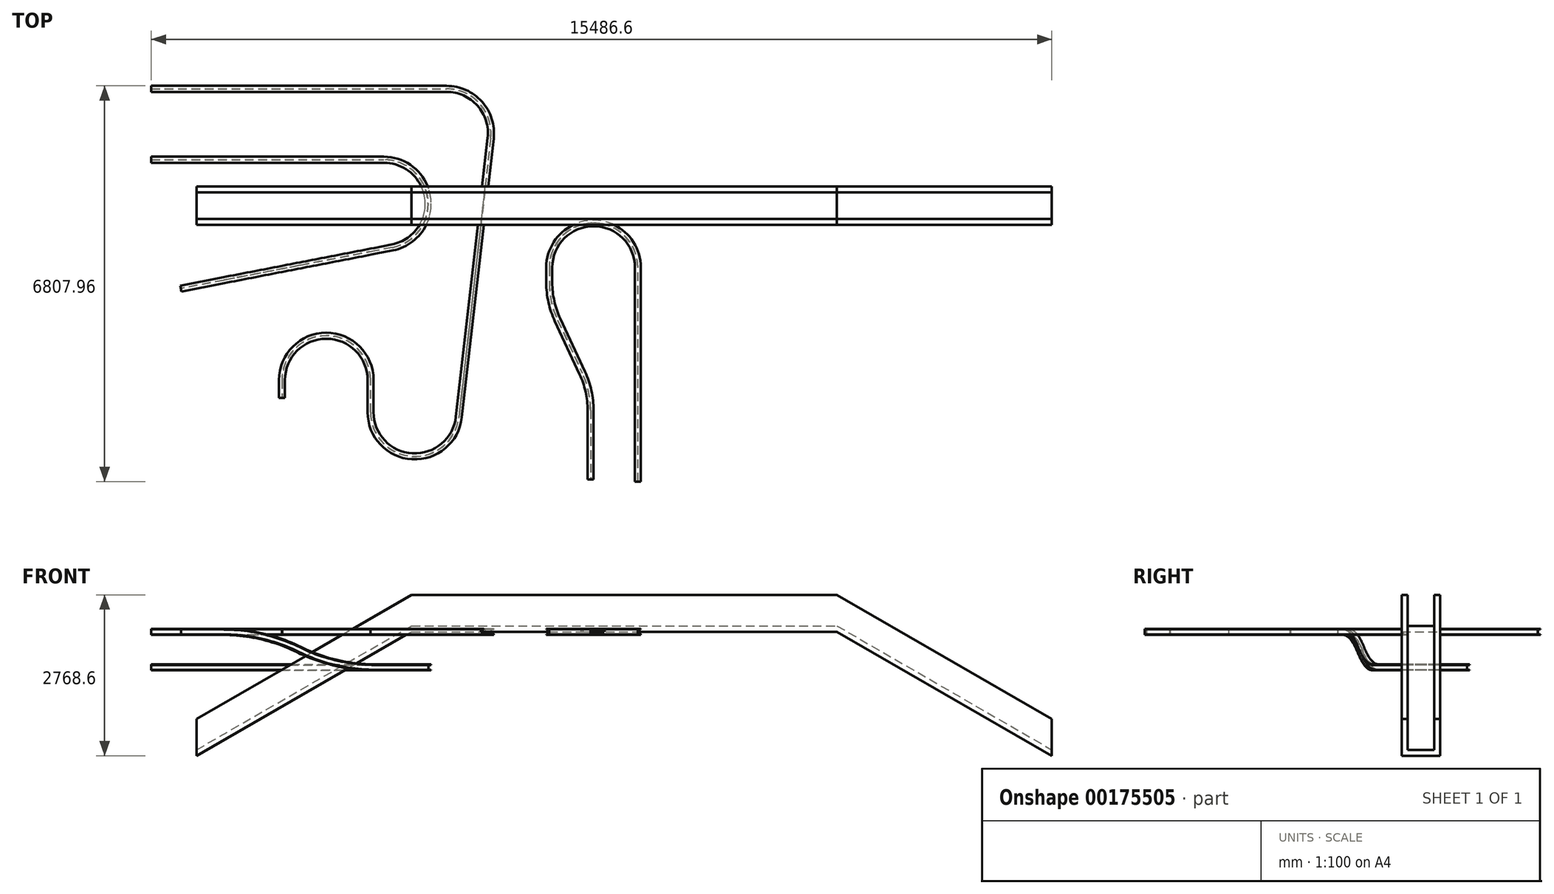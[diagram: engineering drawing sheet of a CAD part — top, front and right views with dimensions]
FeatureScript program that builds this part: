
annotation { "Feature Type Name" : "Feature", "Feature Type Description" : "" }
export const myFeature = defineFeature(function(context is Context, id is Id, definition is map)
    precondition{}
    {
        {
            var Q0;
            Q0=qCreatedBy(makeId("Right.planeOp"),FACE);
            var sketch = newSketch(context, id + "F0", { "sketchPlane" : qUnion([Q0])});
            skLineSegment(sketch, "E0", {"start": v(-3.56, -43.3) * mm, "end": v(-3.56, 43.3) * mm});
            skLineSegment(sketch, "E1", {"start": v(-3.56, 43.3) * mm, "end": v(-51.56, 43.3) * mm});
            skLineSegment(sketch, "E2", {"start": v(-51.56, 43.3) * mm, "end": v(-51.56, 52.83) * mm});
            skLineSegment(sketch, "E3", {"start": v(-51.56, 52.83) * mm, "end": v(51.56, 52.83) * mm});
            skLineSegment(sketch, "E4", {"start": v(51.56, 52.83) * mm, "end": v(51.56, 43.3) * mm});
            skLineSegment(sketch, "E5", {"start": v(51.56, 43.3) * mm, "end": v(3.56, 43.3) * mm});
            skLineSegment(sketch, "E6", {"start": v(3.56, 43.3) * mm, "end": v(3.56, -43.3) * mm});
            skLineSegment(sketch, "E7", {"start": v(3.56, -43.3) * mm, "end": v(51.56, -43.3) * mm});
            skLineSegment(sketch, "E8", {"start": v(51.56, -43.3) * mm, "end": v(51.56, -52.83) * mm});
            skLineSegment(sketch, "E9", {"start": v(51.56, -52.83) * mm, "end": v(-51.56, -52.83) * mm});
            skLineSegment(sketch, "E10", {"start": v(-51.56, -52.83) * mm, "end": v(-51.56, -43.3) * mm});
            skLineSegment(sketch, "E11", {"start": v(-51.56, -43.3) * mm, "end": v(-3.56, -43.3) * mm});
            skSolve(sketch);
        }
        {
            var Q0;
            Q0=qCreatedBy(makeId("Top.planeOp"),FACE);
            var sketch = newSketch(context, id + "F1", { "sketchPlane" : qUnion([Q0])});
            skLineSegment(sketch, "E12", {"start": v(0, 0) * mm, "end": v(5080, 0) * mm});
            skArc(sketch, "E13", {"start": v(5837.12, -848.13) * mm, "mid": v(5648.45, -254.55) * mm, "end": v(5080, 0) * mm});
            skPoint(sketch, "E14", {"position": v(4533.9, -5562.6) * mm});
            skArc(sketch, "E15", {"start": v(3771.9, -5562.6) * mm, "mid": v(4490.77, -6323.38) * mm, "end": v(5291.02, -5648.73) * mm});
            skLineSegment(sketch, "E16", {"start": v(5837.12, -848.13) * mm, "end": v(5291.02, -5648.73) * mm});
            skLineSegment(sketch, "E17", {"start": v(4533.9, -5562.6) * mm, "end": v(3553.98, -5562.6) * mm, "construction": true});
            skPoint(sketch, "E18", {"position": v(3009.9, -5010.15) * mm});
            skLineSegment(sketch, "E19", {"start": v(3771.9, -5562.6) * mm, "end": v(3771.9, -5010.15) * mm});
            skArc(sketch, "E20", {"start": v(3771.9, -5010.15) * mm, "mid": v(3009.9, -4248.15) * mm, "end": v(2247.9, -5010.15) * mm});
            skLineSegment(sketch, "E21", {"start": v(2247.9, -5010.15) * mm, "end": v(2247.9, -5314.95) * mm});
            skSolve(sketch);
        }
        {
            var Q0;
            Q0 = qSketchRegion(id + "F0", true);
            var Q1;
            Q1=sQuery(id+"F1.wireOp",EDGE,"E12");
            var Q2;
            Q2=sQuery(id+"F1.wireOp",EDGE,"E13");
            var Q3;
            Q3=sQuery(id+"F1.wireOp",EDGE,"E16");
            var Q4;
            Q4=sQuery(id+"F1.wireOp",EDGE,"E15");
            var Q5;
            Q5=sQuery(id+"F1.wireOp",EDGE,"E19");
            var Q6;
            Q6=sQuery(id+"F1.wireOp",EDGE,"E20");
            var Q7;
            Q7=sQuery(id+"F1.wireOp",EDGE,"E21");
            sweep(context, id + "F2", {"profiles" : qUnion([Q0]), "path" : qUnion([Q1, Q2, Q3, Q4, Q5, Q6, Q7])});
        }
        {
            var Q0;
            Q0=qCreatedBy(makeId("Right.planeOp"),FACE);
            var sketch = newSketch(context, id + "F3", { "sketchPlane" : qUnion([Q0])});
            skLineSegment(sketch, "E22", {"start": v(-1219.2, 399.7) * mm, "end": v(-1219.2, -446.14) * mm, "construction": true});
            skLineSegment(sketch, "E23", {"start": v(-902.69, 0) * mm, "end": v(-1653.95, 0) * mm, "construction": true});
            skLineSegment(sketch, "E24", {"start": v(-1215.64, -652.9) * mm, "end": v(-1167.64, -652.9) * mm});
            skLineSegment(sketch, "E25", {"start": v(-1167.64, -662.43) * mm, "end": v(-1167.64, -652.9) * mm});
            skLineSegment(sketch, "E26", {"start": v(-1167.64, -662.43) * mm, "end": v(-1270.76, -662.43) * mm});
            skLineSegment(sketch, "E27", {"start": v(-1270.76, -652.9) * mm, "end": v(-1270.76, -662.43) * mm});
            skLineSegment(sketch, "E28", {"start": v(-1270.76, -652.9) * mm, "end": v(-1222.76, -652.9) * mm});
            skLineSegment(sketch, "E29", {"start": v(-1222.76, -570.36) * mm, "end": v(-1270.76, -570.36) * mm});
            skLineSegment(sketch, "E30", {"start": v(-1270.76, -560.83) * mm, "end": v(-1270.76, -570.36) * mm});
            skLineSegment(sketch, "E31", {"start": v(-1270.76, -560.83) * mm, "end": v(-1167.64, -560.83) * mm});
            skLineSegment(sketch, "E32", {"start": v(-1167.64, -570.36) * mm, "end": v(-1167.64, -560.83) * mm});
            skLineSegment(sketch, "E33", {"start": v(-1167.64, -570.36) * mm, "end": v(-1215.64, -570.36) * mm});
            skLineSegment(sketch, "E34", {"start": v(-1215.64, -570.36) * mm, "end": v(-1215.64, -652.9) * mm});
            skLineSegment(sketch, "E35", {"start": v(-1222.76, -570.36) * mm, "end": v(-1222.76, -652.9) * mm});
            skSolve(sketch);
        }
        {
            var Q0;
            Q0=qCreatedBy(makeId("Top.planeOp"),FACE);
            var sketch = newSketch(context, id + "F4", { "sketchPlane" : qUnion([Q0])});
            skLineSegment(sketch, "E36", {"start": v(0, -1219.2) * mm, "end": v(4000.5, -1219.2) * mm});
            skPoint(sketch, "E37", {"position": v(5080, -762) * mm});
            skArc(sketch, "E38", {"start": v(4145.9, -2729.2) * mm, "mid": v(4759, -1908.17) * mm, "end": v(4000.5, -1219.2) * mm});
            skLineSegment(sketch, "E39", {"start": v(4145.9, -2729.2) * mm, "end": v(3846.7, -2787.36) * mm});
            skLineSegment(sketch, "E40", {"start": v(4000.5, -1981.2) * mm, "end": v(4000.5, -3343.17) * mm, "construction": true});
            skLineSegment(sketch, "E41", {"start": v(4000.5, -1981.2) * mm, "end": v(4145.9, -2729.2) * mm, "construction": true});
            skSolve(sketch);
        }
        {
            var Q0;
            Q0 = qSketchRegion(id + "F3", true);
            var Q1;
            Q1=sQuery(id+"F4.wireOp",EDGE,"E36");
            var Q2;
            Q2=sQuery(id+"F4.wireOp",EDGE,"E38");
            var Q3;
            Q3=sQuery(id+"F4.wireOp",EDGE,"E39");
            sweep(context, id + "F5", {"profiles" : qUnion([Q0]), "path" : qUnion([Q1, Q2, Q3])});
        }
        {
            var Q0;
            Q0=makeQuery(id+"F5.opSweep","SWEPT_FACE",FACE,{"disambiguationData":[OSD([sQuery(id+"F3.wireOp",EDGE,"E34"),sQuery(id+"F4.wireOp",EDGE,"E39")])]});
            var sketch = newSketch(context, id + "F6", { "sketchPlane" : qUnion([Q0])});
            skArc(sketch, "E42", {"start": v(1915.58, -306.83) * mm, "mid": v(2562.62, -534.45) * mm, "end": v(3244.17, -611.63) * mm});
            skLineSegment(sketch, "E43", {"start": v(3244.17, -611.63) * mm, "end": v(3472.86, -611.63) * mm, "construction": true});
            skArc(sketch, "E44", {"start": v(1915.58, -306.83) * mm, "mid": v(1272.56, -80.13) * mm, "end": v(595.23, -2.03) * mm});
            skLineSegment(sketch, "E45", {"start": v(595.23, -2.03) * mm, "end": v(-153.73, 0) * mm});
            skSolve(sketch);
        }
        {
            var Q0;
            Q0=makeQuery(id+"F5.opSweep","CAP_FACE",FACE,{"disambiguationData":[OSD([sQuery(id+"F3.wireOp",EDGE,"E24"),sQuery(id+"F3.wireOp",EDGE,"E25"),sQuery(id+"F3.wireOp",EDGE,"E26"),sQuery(id+"F3.wireOp",EDGE,"E27"),sQuery(id+"F3.wireOp",EDGE,"E28"),sQuery(id+"F3.wireOp",EDGE,"E29"),sQuery(id+"F3.wireOp",EDGE,"E30"),sQuery(id+"F3.wireOp",EDGE,"E31"),sQuery(id+"F3.wireOp",EDGE,"E32"),sQuery(id+"F3.wireOp",EDGE,"E33"),sQuery(id+"F3.wireOp",EDGE,"E34"),sQuery(id+"F3.wireOp",EDGE,"E35"),sQuery(id+"F4.wireOp",VERTEX,"E39.end")])],"isStart":false});
            var Q1;
            Q1=sQuery(id+"F6.wireOp",EDGE,"E42");
            var Q2;
            Q2=sQuery(id+"F6.wireOp",EDGE,"E44");
            var Q3;
            Q3=sQuery(id+"F6.wireOp",EDGE,"E45");
            sweep(context, id + "F7", {"operationType" : NewBodyOperationType.ADD, "profiles" : qUnion([Q0]), "path" : qUnion([Q1, Q2, Q3])});
        }
        {
            var Q0;
            Q0=qCreatedBy(makeId("Front.planeOp"),FACE);
            cPlane(context, id + "F8", {"entities" : qUnion([Q0]), "cplaneType" : CPlaneType.OFFSET, "offset" : 2336.8 * mm, "width" : 152.4 * mm, "height" : 152.4 * mm});
        }
        {
            var Q0;
            Q0=qCreatedBy(id+"F8.planeOp",FACE);
            var sketch = newSketch(context, id + "F9", { "sketchPlane" : qUnion([Q0])});
            skLineSegment(sketch, "E46", {"start": v(781.05, -2131.57) * mm, "end": v(4476.75, 2.03) * mm});
            skLineSegment(sketch, "E47", {"start": v(4476.75, 2.03) * mm, "end": v(11791.95, 2.03) * mm});
            skLineSegment(sketch, "E48", {"start": v(11791.95, 2.03) * mm, "end": v(15487.65, -2131.57) * mm});
            skSolve(sketch);
        }
        {
            var Q0;
            Q0=qCreatedBy(makeId("Right.planeOp"),FACE);
            cPlane(context, id + "F10", {"entities" : qUnion([Q0]), "cplaneType" : CPlaneType.OFFSET, "offset" : 780 * mm, "width" : 152.4 * mm, "height" : 152.4 * mm});
        }
        {
            var Q0;
            Q0=qCreatedBy(id+"F10.planeOp",FACE);
            var sketch = newSketch(context, id + "F11", { "sketchPlane" : qUnion([Q0])});
            skLineSegment(sketch, "E49", {"start": v(-2336.8, -2131.57) * mm, "end": v(-2336.8, -1496.57) * mm});
            skLineSegment(sketch, "E50", {"start": v(-2336.8, -1496.57) * mm, "end": v(-2235.2, -1496.57) * mm});
            skLineSegment(sketch, "E51", {"start": v(-2235.2, -1496.57) * mm, "end": v(-2235.2, -2029.97) * mm});
            skLineSegment(sketch, "E52", {"start": v(-2235.2, -2029.97) * mm, "end": v(-1778, -2029.97) * mm});
            skLineSegment(sketch, "E53", {"start": v(-1778, -2029.97) * mm, "end": v(-1778, -1496.57) * mm});
            skLineSegment(sketch, "E54", {"start": v(-1778, -1496.57) * mm, "end": v(-1676.4, -1496.57) * mm});
            skLineSegment(sketch, "E55", {"start": v(-1676.4, -1496.57) * mm, "end": v(-1676.4, -2131.57) * mm});
            skLineSegment(sketch, "E56", {"start": v(-1676.4, -2131.57) * mm, "end": v(-2336.8, -2131.57) * mm});
            skSolve(sketch);
        }
        {
            var Q0;
            Q0=makeQuery(id+"F11.imprint","IMPRINT",FACE,{"disambiguationData":[TD([[makeQuery(id+"F11.imprint","IMPRINT",EDGE,{"derivedFrom":sQuery(id+"F11.wireOp",EDGE,"E49")}),-1.0]])]});
            var Q1;
            Q1=sQuery(id+"F9.wireOp",EDGE,"E46");
            var Q2;
            Q2=sQuery(id+"F9.wireOp",EDGE,"E47");
            var Q3;
            Q3=sQuery(id+"F9.wireOp",EDGE,"E48");
            sweep(context, id + "F12", {"operationType" : NewBodyOperationType.ADD, "profiles" : qUnion([Q0]), "path" : qUnion([Q1, Q2, Q3]), "keepProfileOrientation" : true});
        }
        {
            var Q0;
            Q0=qCreatedBy(makeId("Top.planeOp"),FACE);
            var sketch = newSketch(context, id + "F13", { "sketchPlane" : qUnion([Q0])});
            skPoint(sketch, "E57", {"position": v(5080, -762) * mm});
            skPoint(sketch, "E58", {"position": v(7607.3, -3073.4) * mm});
            skArc(sketch, "E59", {"start": v(6845.3, -3073.4) * mm, "mid": v(7607.3, -2311.4) * mm, "end": v(8369.3, -3073.4) * mm});
            skLineSegment(sketch, "E60", {"start": v(8369.3, -3073.4) * mm, "end": v(8369.3, -6756.4) * mm});
            skLineSegment(sketch, "E61", {"start": v(6845.3, -3073.4) * mm, "end": v(6845.3, -3332.44) * mm});
            skLineSegment(sketch, "E62", {"start": v(6988.09, -3976.5) * mm, "end": v(7413.17, -4888.1) * mm});
            skLineSegment(sketch, "E63", {"start": v(7555.95, -5532.16) * mm, "end": v(7555.95, -6718.3) * mm});
            skPoint(sketch, "E64.visualSharp", {"position": v(6845.3, -3670.3) * mm});
            skArc(sketch, "E64.filletArc", {"start": v(6845.3, -3332.44) * mm, "mid": v(6881.42, -3662.3) * mm, "end": v(6988.09, -3976.5) * mm});
            skPoint(sketch, "E65.visualSharp", {"position": v(7555.95, -5194.3) * mm});
            skArc(sketch, "E65.filletArc", {"start": v(7555.95, -5532.16) * mm, "mid": v(7519.83, -5202.3) * mm, "end": v(7413.17, -4888.1) * mm});
            skSolve(sketch);
        }
        {
            var Q0;
            Q0=sQuery(id+"F13.wireOp",VERTEX,"E60.end");
            var Q1;
            Q1=qCreatedBy(makeId("Front.planeOp"),FACE);
            cPlane(context, id + "F14", {"entities" : qUnion([Q0, Q1]), "cplaneType" : CPlaneType.PLANE_POINT, "offset" : 25.4 * mm, "width" : 152.4 * mm, "height" : 152.4 * mm});
        }
        {
            var Q0;
            Q0=qCreatedBy(id+"F14.planeOp",FACE);
            var sketch = newSketch(context, id + "F15", { "sketchPlane" : qUnion([Q0])});
            skLineSegment(sketch, "E66", {"start": v(8372.86, -43.3) * mm, "end": v(8372.86, 43.3) * mm});
            skLineSegment(sketch, "E67", {"start": v(8372.86, 43.3) * mm, "end": v(8420.86, 43.3) * mm});
            skLineSegment(sketch, "E68", {"start": v(8420.86, 43.3) * mm, "end": v(8420.86, 52.83) * mm});
            skLineSegment(sketch, "E69", {"start": v(8420.86, 52.83) * mm, "end": v(8317.74, 52.83) * mm});
            skLineSegment(sketch, "E70", {"start": v(8317.74, 52.83) * mm, "end": v(8317.74, 43.3) * mm});
            skLineSegment(sketch, "E71", {"start": v(8317.74, 43.3) * mm, "end": v(8365.74, 43.3) * mm});
            skLineSegment(sketch, "E72", {"start": v(8365.74, 43.3) * mm, "end": v(8365.74, -43.3) * mm});
            skLineSegment(sketch, "E73", {"start": v(8365.74, -43.3) * mm, "end": v(8317.74, -43.3) * mm});
            skLineSegment(sketch, "E74", {"start": v(8317.74, -43.3) * mm, "end": v(8317.74, -52.83) * mm});
            skLineSegment(sketch, "E75", {"start": v(8317.74, -52.83) * mm, "end": v(8420.86, -52.83) * mm});
            skLineSegment(sketch, "E76", {"start": v(8420.86, -52.83) * mm, "end": v(8420.86, -43.3) * mm});
            skLineSegment(sketch, "E77", {"start": v(8420.86, -43.3) * mm, "end": v(8372.86, -43.3) * mm});
            skSolve(sketch);
        }
        {
            var Q0;
            Q0=makeQuery(id+"F15.imprint","IMPRINT",FACE,{"disambiguationData":[TD([[makeQuery(id+"F15.imprint","IMPRINT",EDGE,{"derivedFrom":sQuery(id+"F15.wireOp",EDGE,"E66")}),1.0]])]});
            var Q1;
            Q1=sQuery(id+"F13.wireOp",EDGE,"E60");
            var Q2;
            Q2=sQuery(id+"F13.wireOp",EDGE,"E59");
            var Q3;
            Q3=sQuery(id+"F13.wireOp",EDGE,"E61");
            var Q4;
            Q4=sQuery(id+"F13.wireOp",EDGE,"E64.filletArc");
            var Q5;
            Q5=sQuery(id+"F13.wireOp",EDGE,"E62");
            var Q6;
            Q6=sQuery(id+"F13.wireOp",EDGE,"E65.filletArc");
            var Q7;
            Q7=sQuery(id+"F13.wireOp",EDGE,"E63");
            sweep(context, id + "F16", {"operationType" : NewBodyOperationType.ADD, "profiles" : qUnion([Q0]), "path" : qUnion([Q1, Q2, Q3, Q4, Q5, Q6, Q7])});
        }
    });
